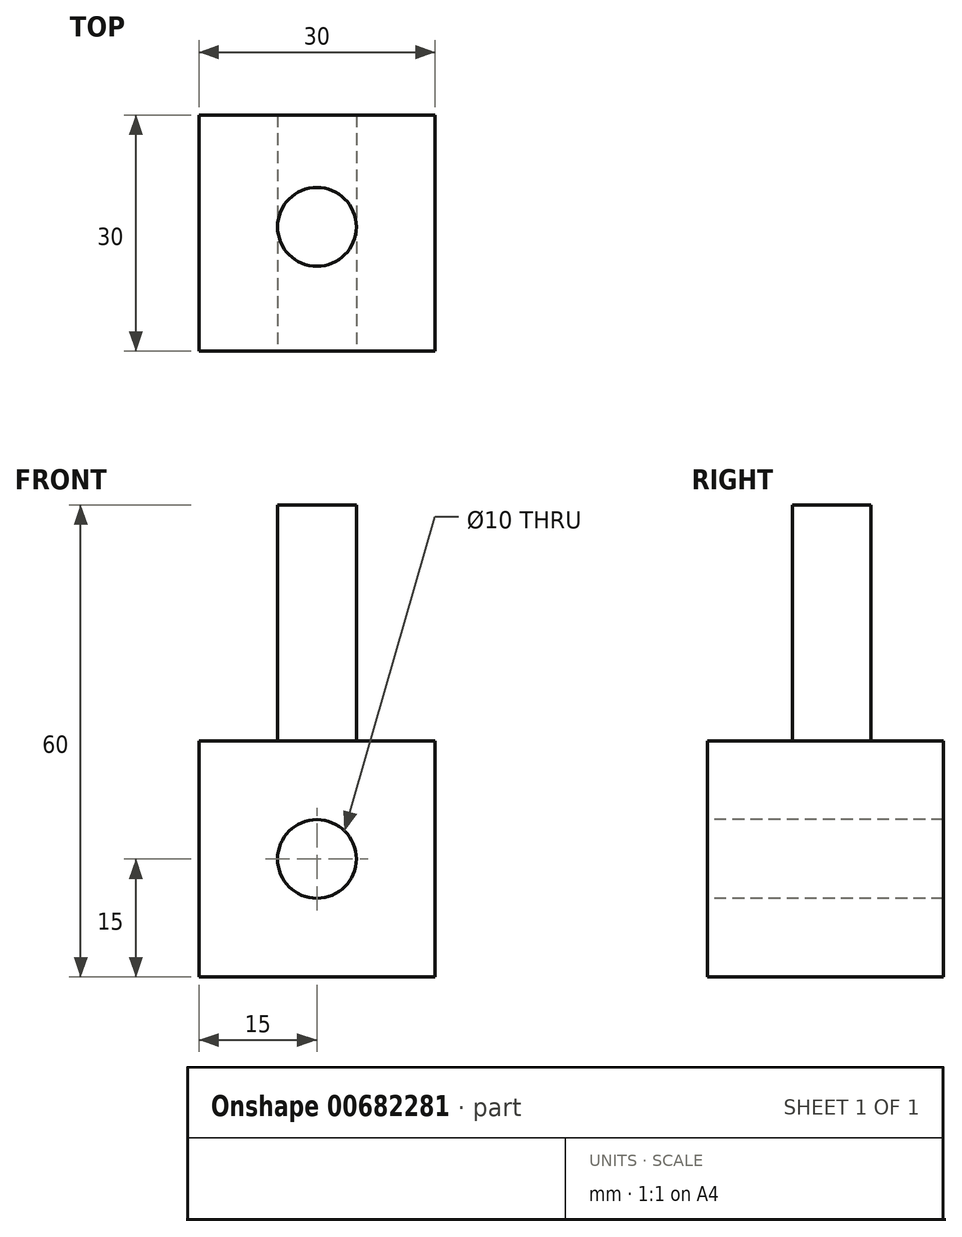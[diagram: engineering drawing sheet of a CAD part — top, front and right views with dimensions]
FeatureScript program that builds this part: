
annotation { "Feature Type Name" : "Feature", "Feature Type Description" : "" }
export const myFeature = defineFeature(function(context is Context, id is Id, definition is map)
    precondition{}
    {
        {
            var Q0;
            Q0=qCreatedBy(makeId("Front.planeOp"),FACE);
            var sketch = newSketch(context, id + "F0", { "sketchPlane" : qUnion([Q0])});
            skLineSegment(sketch, "E0.bottom", {"start": v(15, 15) * mm, "end": v(-15, 15) * mm});
            skLineSegment(sketch, "E0.top", {"start": v(15, -15) * mm, "end": v(-15, -15) * mm});
            skLineSegment(sketch, "E0.left", {"start": v(15, 15) * mm, "end": v(15, -15) * mm});
            skLineSegment(sketch, "E0.right", {"start": v(-15, 15) * mm, "end": v(-15, -15) * mm});
            skPoint(sketch, "E0.middle", {"position": v(0, 0) * mm});
            skSolve(sketch);
        }
        {
            var Q0;
            Q0 = qSketchRegion(id + "F0", true);
            extrude(context, id + "F1", {"entities" : qUnion([Q0]), "depth" : 30 * mm, "offsetDistance" : 25 * mm});
        }
        {
            var Q0;
            Q0=makeQuery(id+"F1.opExtrude","CAP_FACE",FACE,{"disambiguationData":[OSD([sQuery(id+"F0.wireOp",EDGE,"E0.bottom"),sQuery(id+"F0.wireOp",EDGE,"E0.top"),sQuery(id+"F0.wireOp",EDGE,"E0.left"),sQuery(id+"F0.wireOp",EDGE,"E0.right")])],"isStart":false});
            var sketch = newSketch(context, id + "F2", { "sketchPlane" : qUnion([Q0])});
            skCircle(sketch, "E1", {"center": v(0, 0) * mm, "radius": 5 * mm});
            skSolve(sketch);
        }
        {
            var Q0;
            Q0=makeQuery(id+"F2.imprint","IMPRINT",FACE,{"disambiguationData":[TD([[makeQuery(id+"F2.imprint","IMPRINT",EDGE,{"derivedFrom":sQuery(id+"F2.wireOp",EDGE,"E1")}),1.0]])]});
            extrude(context, id + "F3", {"entities" : qUnion([Q0]), "operationType" : NewBodyOperationType.REMOVE, "oppositeDirection" : true, "depth" : 35 * mm, "offsetDistance" : 25 * mm});
        }
        {
            var Q0;
            Q0=makeQuery(id+"F1.opExtrude","SWEPT_FACE",FACE,{"disambiguationData":[OSD([sQuery(id+"F0.wireOp",EDGE,"E0.bottom")])]});
            var sketch = newSketch(context, id + "F4", { "sketchPlane" : qUnion([Q0])});
            skCircle(sketch, "E2", {"center": v(0, -14.2) * mm, "radius": 5 * mm});
            skSolve(sketch);
        }
        {
            var Q0;
            Q0=makeQuery(id+"F4.imprint","IMPRINT",FACE,{"disambiguationData":[TD([[makeQuery(id+"F4.imprint","IMPRINT",EDGE,{"derivedFrom":sQuery(id+"F4.wireOp",EDGE,"E2")}),1.0]])]});
            var Q1;
            Q1=sQuery(id+"F4.wireOp",EDGE,"E2");
            extrude(context, id + "F5", {"entities" : qUnion([Q0]), "operationType" : NewBodyOperationType.ADD, "surfaceEntities" : qUnion([Q1]), "depth" : 30 * mm, "offsetDistance" : 25 * mm});
        }
    });
